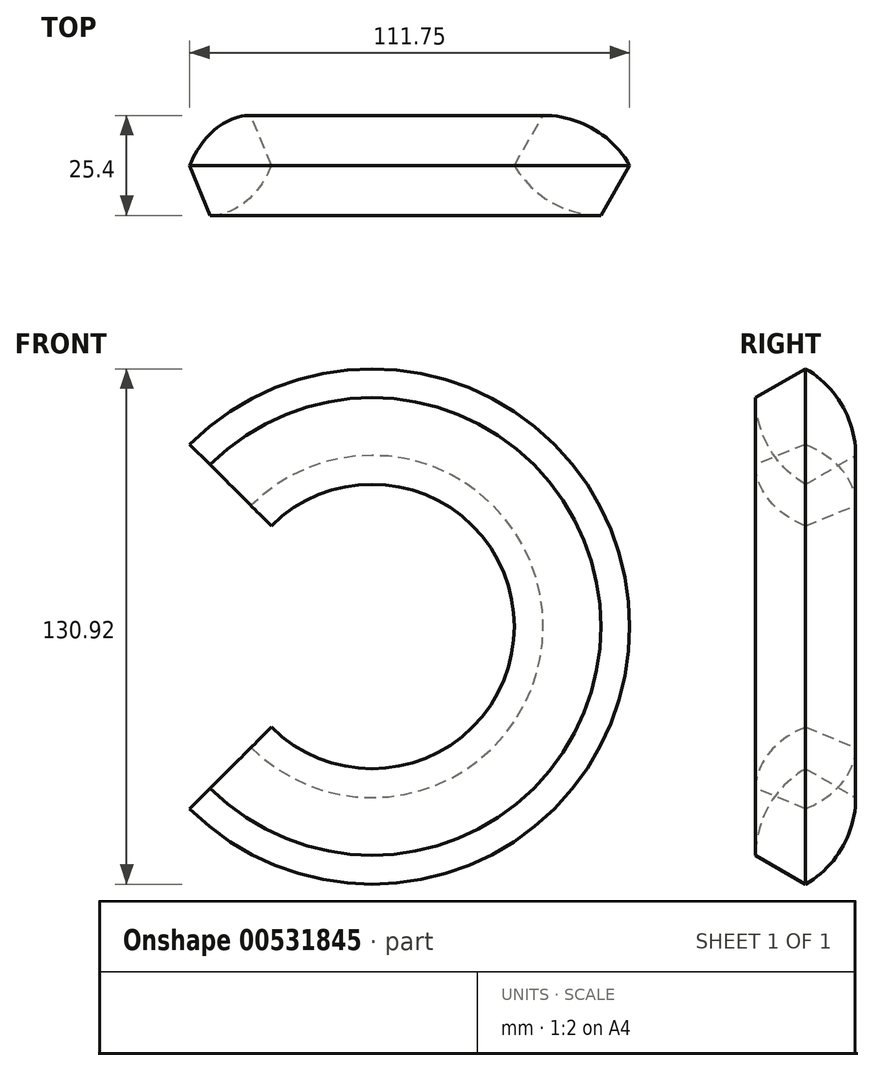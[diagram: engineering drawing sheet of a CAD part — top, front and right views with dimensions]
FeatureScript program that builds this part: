
annotation { "Feature Type Name" : "Feature", "Feature Type Description" : "" }
export const myFeature = defineFeature(function(context is Context, id is Id, definition is map)
    precondition{}
    {
        {
            var Q0;
            Q0=qCreatedBy(makeId("Top.planeOp"),FACE);
            var sketch = newSketch(context, id + "F0", { "sketchPlane" : qUnion([Q0])});
            skCircle(sketch, "E0.cCircle", {"center": v(0, 0) * mm, "radius": 12.7 * mm, "construction": true});
            skLineSegment(sketch, "E0.0", {"start": v(7.33, 12.7) * mm, "end": v(14.66, 0) * mm});
            skLineSegment(sketch, "E0.1", {"start": v(14.66, 0) * mm, "end": v(7.33, -12.7) * mm});
            skLineSegment(sketch, "E0.2", {"start": v(7.33, -12.7) * mm, "end": v(-7.33, -12.7) * mm});
            skLineSegment(sketch, "E0.3", {"start": v(-7.33, -12.7) * mm, "end": v(-14.66, 0) * mm});
            skLineSegment(sketch, "E0.4", {"start": v(-14.66, 0) * mm, "end": v(-7.33, 12.7) * mm});
            skLineSegment(sketch, "E0.5", {"start": v(-7.33, 12.7) * mm, "end": v(7.33, 12.7) * mm});
            skPoint(sketch, "E0.0.midPoint", {"position": v(11, 6.35) * mm});
            skLineSegment(sketch, "E1", {"start": v(-50.8, 24.54) * mm, "end": v(-50.8, -25.94) * mm, "construction": true});
            skSolve(sketch);
        }
        {
            var Q0;
            Q0 = qSketchRegion(id + "F0", true);
            var Q1;
            Q1=sQuery(id+"F0.wireOp",EDGE,"E1");
            revolve(context, id + "F1", {"entities" : qUnion([Q0]), "axis" : qUnion([Q1]), "revolveType" : RevolveType.SYMMETRIC, "angle" : 270 * degree});
        }
        {
            var Q0;
            Q0=makeQuery(id+"F1.opRevolve","SWEPT_EDGE",EDGE,{"disambiguationData":[OSD([sQuery(id+"F0.wireOp",EDGE,"E0.0"),sQuery(id+"F0.wireOp",EDGE,"E0.5")])]});
            var Q1;
            Q1=makeQuery(id+"F1.opRevolve","SWEPT_EDGE",EDGE,{"disambiguationData":[OSD([sQuery(id+"F0.wireOp",EDGE,"E0.2"),sQuery(id+"F0.wireOp",EDGE,"E0.3")])]});
            fillet(context, id + "F2", {"entities" : qUnion([Q0, Q1]), "radius" : 25.4 * mm, "tangentPropagation" : true, "allowEdgeOverflow" : false});
        }
    });
